# Revit family: Furniture-Floor_Mount-Vanity-KOHLER-Artifacts-K-33559
name_source: partatom
category: Casework
units: mm (PartAtom-declared; Revit-internal decimal feet)

## family parameters
Cut with Voids When Loaded = No
Host = Face
OmniClass Number = 23.21.19.15.33
OmniClass Title = Residential Specialty Casework
Room Calculation Point = No
Shared = No

## types (5) — shared parameters
ADA Compliant = No
Assembly Code = E2010.30
Construction Type = Floor Mount
Date Modified = 02/05/2025
Default Elevation = 0"
Depth = 21 7/8"
Description = 36 Inch Bathroom Vanity Cabinet
Hardware Included = No
Height = 34 1/2"
Manufacturer = Kohler Co.
Master Format 2014 = 12 35 30.23
Master Format 2014 Name = Bathroom Casework
Material = Solid Wood
Product Documentation Link = https://www.us.kohler.com
Product Name = Artifacts
Product Page URL = http://www.us.kohler.com
URL = https://www.us.kohler.com
WaterSense Certified = No
Width = 36"

## per-type parameters (varying)
| type | Finish | Model | Product Finish | Type |
| 1WA-Linen White | Kohler-Wood-1WA-Linen White | K-33559-1WA | Kohler-Wood-1WA-Linen_White | 1 |
| 1WX-New Dark Grey | Kohler-Wood-1WX-New_Dark_Grey | K-33559-1WX | KOHLER-Wood-1WX-New_Dark_Grey | 2 |
| AGA-Ash Grey | KOHLER-Wood-AGA-Ash_Grey | K-33559-AGA | KOHLER-Wood-AGA-Ash_Grey | 3 |
| BWK-Carbon Oak | KOHLER-Wood-BWK-Carbon_Oak | K-33559-BWK | KOHLER-Wood-BWK-Carbon_Oak | 4 |
| WEK-Weathered Oak | KOHLER-Wood-WEK-Weathered_Oak | K-33559-WEK | KOHLER-Wood-WEK-Weathered_Oak | 5 |

## geometry (parser evidence)
native form markers: Sweep x5
no freeform markers — native parametric forms only
